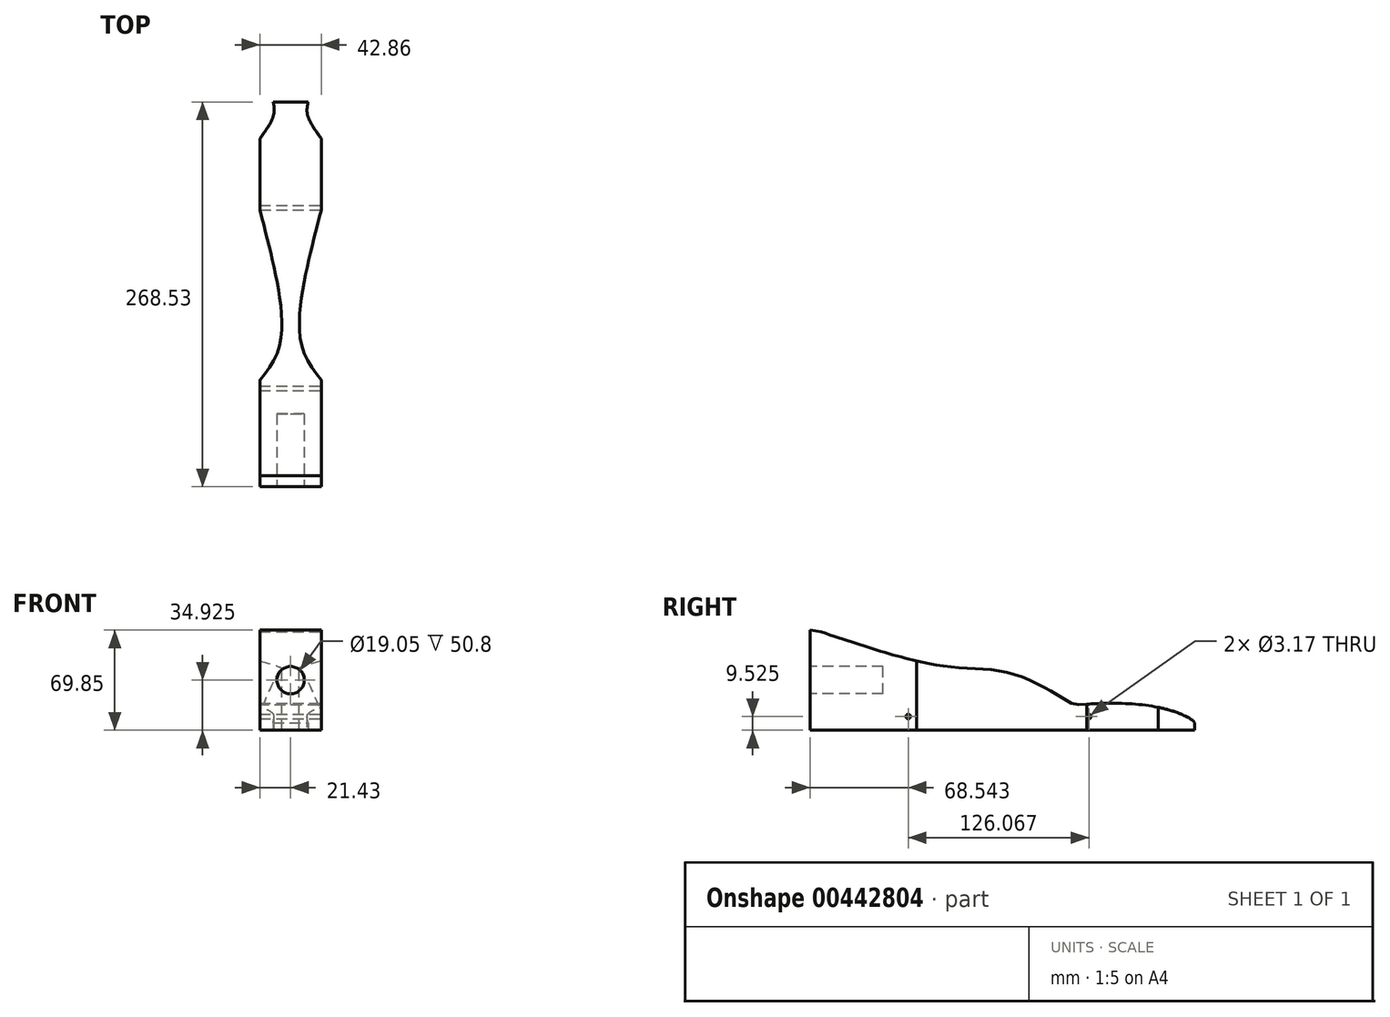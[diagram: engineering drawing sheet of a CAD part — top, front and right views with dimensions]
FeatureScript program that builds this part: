
annotation { "Feature Type Name" : "Feature", "Feature Type Description" : "" }
export const myFeature = defineFeature(function(context is Context, id is Id, definition is map)
    precondition{}
    {
        {
            var Q0;
            Q0=qCreatedBy(makeId("Right.planeOp"),FACE);
            var sketch = newSketch(context, id + "F0", { "sketchPlane" : qUnion([Q0])});
            skLineSegment(sketch, "E0", {"start": v(-152.4, 0) * mm, "end": v(152.4, 0) * mm});
            skLineSegment(sketch, "E1", {"start": v(-152.4, 0) * mm, "end": v(-152.4, 69.85) * mm});
            skLineSegment(sketch, "E2", {"start": v(152.4, 0) * mm, "end": v(152.4, 19.05) * mm});
            skLineSegment(sketch, "E3", {"start": v(152.4, 19.05) * mm, "end": v(-152.4, 69.85) * mm});
            skPoint(sketch, "E4.endSnap0", {"position": v(-152.4, 34.93) * mm});
            skLineSegment(sketch, "E5.0", {"start": v(-95.25, 50.8) * mm, "end": v(-152.4, 50.8) * mm, "construction": true});
            skLineSegment(sketch, "E5.1", {"start": v(-95.25, 50.8) * mm, "end": v(-95.25, 19.05) * mm, "construction": true});
            skLineSegment(sketch, "E5.2", {"start": v(-95.25, 19.05) * mm, "end": v(-152.4, 19.05) * mm, "construction": true});
            skSolve(sketch);
        }
        {
            var Q0;
            Q0=makeQuery(id+"F0.imprint","IMPRINT",FACE,{"disambiguationData":[TD([[makeQuery(id+"F0.imprint","IMPRINT",EDGE,{"derivedFrom":sQuery(id+"F0.wireOp",EDGE,"E0")}),1.0]])]});
            extrude(context, id + "F1", {"entities" : qUnion([Q0]), "depth" : 42.86 * mm, "symmetric" : true});
        }
        {
            var Q0;
            Q0=makeQuery(id+"F1.opExtrude","SWEPT_FACE",FACE,{"disambiguationData":[OSD([sQuery(id+"F0.wireOp",EDGE,"E1")])]});
            var sketch = newSketch(context, id + "F2", { "sketchPlane" : qUnion([Q0])});
            skLineSegment(sketch, "E6", {"start": v(21.43, 34.93) * mm, "end": v(0, 34.93) * mm, "construction": true});
            skCircle(sketch, "E7", {"center": v(0, 34.93) * mm, "radius": 9.53 * mm});
            skSolve(sketch);
        }
        {
            var Q0;
            Q0=makeQuery(id+"F2.imprint","IMPRINT",FACE,{"disambiguationData":[TD([[makeQuery(id+"F2.imprint","IMPRINT",EDGE,{"derivedFrom":sQuery(id+"F2.wireOp",EDGE,"E7")}),1.0]])]});
            var Q1;
            Q1=sQuery(id+"F2.wireOp",EDGE,"E7");
            extrude(context, id + "F3", {"entities" : qUnion([Q0]), "operationType" : NewBodyOperationType.REMOVE, "surfaceEntities" : qUnion([Q1]), "oppositeDirection" : true, "depth" : 50.8 * mm});
        }
        {
            var Q0;
            Q0=makeQuery(id+"F1.opExtrude","CAP_FACE",FACE,{"disambiguationData":[OSD([sQuery(id+"F0.wireOp",EDGE,"E0"),sQuery(id+"F0.wireOp",EDGE,"E1"),sQuery(id+"F0.wireOp",EDGE,"E2"),sQuery(id+"F0.wireOp",EDGE,"E3")])],"isStart":false});
            var sketch = newSketch(context, id + "F4", { "sketchPlane" : qUnion([Q0])});
            skLineSegment(sketch, "E8", {"start": v(-152.4, 34.93) * mm, "end": v(-152.4, 44.45) * mm, "construction": true});
            skLineSegment(sketch, "E9.0", {"start": v(-95.25, 19.05) * mm, "end": v(-152.4, 19.05) * mm, "construction": true});
            skLineSegment(sketch, "E9.1", {"start": v(-95.25, 50.8) * mm, "end": v(-95.25, 19.05) * mm, "construction": true});
            skLineSegment(sketch, "E9.2", {"start": v(-152.4, 50.8) * mm, "end": v(-95.25, 50.8) * mm, "construction": true});
            skLineSegment(sketch, "E10", {"start": v(57.15, 0) * mm, "end": v(57.15, 34.93) * mm, "construction": true});
            skLineSegment(sketch, "E11", {"start": v(-152.4, 44.45) * mm, "end": v(-101.6, 44.45) * mm, "construction": true});
            skLineSegment(sketch, "E12", {"start": v(-101.6, 44.45) * mm, "end": v(-101.6, 25.4) * mm, "construction": true});
            skLineSegment(sketch, "E13", {"start": v(-101.6, 25.4) * mm, "end": v(-152.4, 25.4) * mm, "construction": true});
            skPoint(sketch, "E14.1.internal.snap0", {"position": v(-127, 44.45) * mm});
            skPoint(sketch, "E14.3.internal.snap0", {"position": v(57.15, 17.46) * mm});
            skPoint(sketch, "E14.4.internal.snap0", {"position": v(57.15, 17.46) * mm});
            skPoint(sketch, "E14.5.internal.snap0", {"position": v(57.15, 17.46) * mm});
            skFitSpline(sketch, "E14", {"points": [v(-144.61, 68.55) * mm, v(-57.04, 44.45) * mm, v(-6.27, 37.78) * mm, v(32.52, 17.46) * mm, v(33.09, 17.46) * mm, v(81.57, 17.46) * mm, v(116.37, 4.7) * mm, v(116.37, 0) * mm], "startDerivative": vector(390.18, -130.64) * mm, "endDerivative": vector(-26.3, -82.43) * mm});
            skCircle(sketch, "E15", {"center": v(-83.86, 9.53) * mm, "radius": 1.59 * mm});
            skCircle(sketch, "E16", {"center": v(42.21, 9.53) * mm, "radius": 1.59 * mm});
            skSolve(sketch);
        }
        {
            var Q0;
            Q0=makeQuery(id+"F1.opExtrude","SWEPT_FACE",FACE,{"disambiguationData":[OSD([sQuery(id+"F0.wireOp",EDGE,"E0")])]});
            var sketch = newSketch(context, id + "F5", { "sketchPlane" : qUnion([Q0])});
            skLineSegment(sketch, "E17", {"start": v(0, 152.4) * mm, "end": v(0, -152.4) * mm, "construction": true});
            skLineSegment(sketch, "E18", {"start": v(21.43, -57.15) * mm, "end": v(-21.43, -57.15) * mm, "construction": true});
            skLineSegment(sketch, "E19", {"start": v(15.88, 152.4) * mm, "end": v(15.88, 95.25) * mm, "construction": true});
            skLineSegment(sketch, "E20", {"start": v(15.88, 95.25) * mm, "end": v(-15.87, 95.25) * mm, "construction": true});
            skLineSegment(sketch, "E21", {"start": v(-15.87, 95.25) * mm, "end": v(-15.87, 152.4) * mm, "construction": true});
            skLineSegment(sketch, "E22", {"start": v(0, 152.4) * mm, "end": v(-9.53, 152.4) * mm, "construction": true});
            skLineSegment(sketch, "E23", {"start": v(-9.53, 152.4) * mm, "end": v(-9.53, 101.6) * mm, "construction": true});
            skLineSegment(sketch, "E24", {"start": v(-9.52, 101.6) * mm, "end": v(9.53, 101.6) * mm, "construction": true});
            skLineSegment(sketch, "E25", {"start": v(9.53, 101.6) * mm, "end": v(9.53, 152.4) * mm, "construction": true});
            skFitSpline(sketch, "E26", {"points": [v(-21.43, 78.01) * mm, v(-6.78, 49.52) * mm, v(-21.43, -40.7) * mm], "startDerivative": vector(51.05, -64.16) * mm, "endDerivative": vector(-43.01, -164.69) * mm});
            skFitSpline(sketch, "E27.MirrorCS", {"points": [v(21.43, 78.01) * mm, v(6.78, 49.52) * mm, v(21.43, -40.7) * mm], "startDerivative": vector(-51.05, -64.16) * mm, "endDerivative": vector(43.01, -164.69) * mm});
            skFitSpline(sketch, "E28", {"points": [v(-12.17, -116.13) * mm, v(-11.93, -106.77) * mm, v(-21.43, -90.46) * mm], "startDerivative": vector(4.05, 21.57) * mm, "endDerivative": vector(-21.11, 29.3) * mm});
            skFitSpline(sketch, "E29.MirrorCS", {"points": [v(12.17, -116.13) * mm, v(11.93, -106.77) * mm, v(21.43, -90.46) * mm], "startDerivative": vector(-4.05, 21.57) * mm, "endDerivative": vector(21.11, 29.3) * mm});
            skLineSegment(sketch, "E30", {"start": v(-12.17, -116.13) * mm, "end": v(12.17, -116.13) * mm});
            skSolve(sketch);
        }
        {
            var Q0;
            {var subQ1=sQuery(id+"F4.wireOp",EDGE,"E14");Q0=makeQuery(id+"F4.imprint","IMPRINT",FACE,{"disambiguationData":[TD([[makeQuery(id+"F4.imprint","IMPRINT",EDGE,{"derivedFrom":subQ1}),-1.0]])]});}
            extrude(context, id + "F6", {"entities" : qUnion([Q0]), "operationType" : NewBodyOperationType.INTERSECT, "endBound" : BoundingType.THROUGH_ALL, "oppositeDirection" : true, "depth" : 25.4 * mm});
        }
        {
            var Q0;
            {var subQ5=sQuery(id+"F5.wireOp",EDGE,"E26");Q0=makeQuery(id+"F5.imprint","IMPRINT",FACE,{"disambiguationData":[TD([[makeQuery(id+"F5.imprint","IMPRINT",EDGE,{"derivedFrom":subQ5}),1.0]])]});}
            extrude(context, id + "F7", {"entities" : qUnion([Q0]), "operationType" : NewBodyOperationType.INTERSECT, "endBound" : BoundingType.THROUGH_ALL, "oppositeDirection" : true, "depth" : 25.4 * mm});
        }
    });
